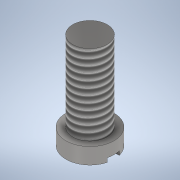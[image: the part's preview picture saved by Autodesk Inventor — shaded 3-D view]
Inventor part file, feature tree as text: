
AUTODESK INVENTOR PART (.ipt)
format: ipt  version: 2020 (Build 240168000, 168)  size: 130,048 bytes
history: native  units: in
note: dims shown in document units (in); Inventor stores cm internally (conversion verified against a paired STEP export)
features: extrude x3, sketch x3, thread x1
ambient origin geometry x8: Origin, YZ Plane, XZ Plane, XY Plane, X Axis, Y Axis, Z Axis, Center Point
bodies: Solid1 (feature_tree)
feature tree (7):
  extrude  "Extrusion1"  Depth=0.0394in TaperAngle=0.0deg
  extrude  "Extrusion2"  Depth=0.1969in TaperAngle=0.0deg
  thread  "Thread1"  [1 undecoded]
  extrude  "Extrusion3"  Depth=0.0098in
  sketch  "Sketch1"  dims[d0=0.1181in d1=0.0394in d2=0.0in]
  sketch  "Sketch2"  dims[d3=0.0849in d4=0.1969in d5=0.0in d6=0.1969in d7=0.0in]
  sketch  "Sketch3"  dims[d8=0.0295in d9=0.0148in d10=0.0098in d11=0.0in]
note: 1 required parameter value undecoded (feature->parameter linkage not recoverable at this tier; creation-order binding heuristic only, values carry confidence <= 0.55)
